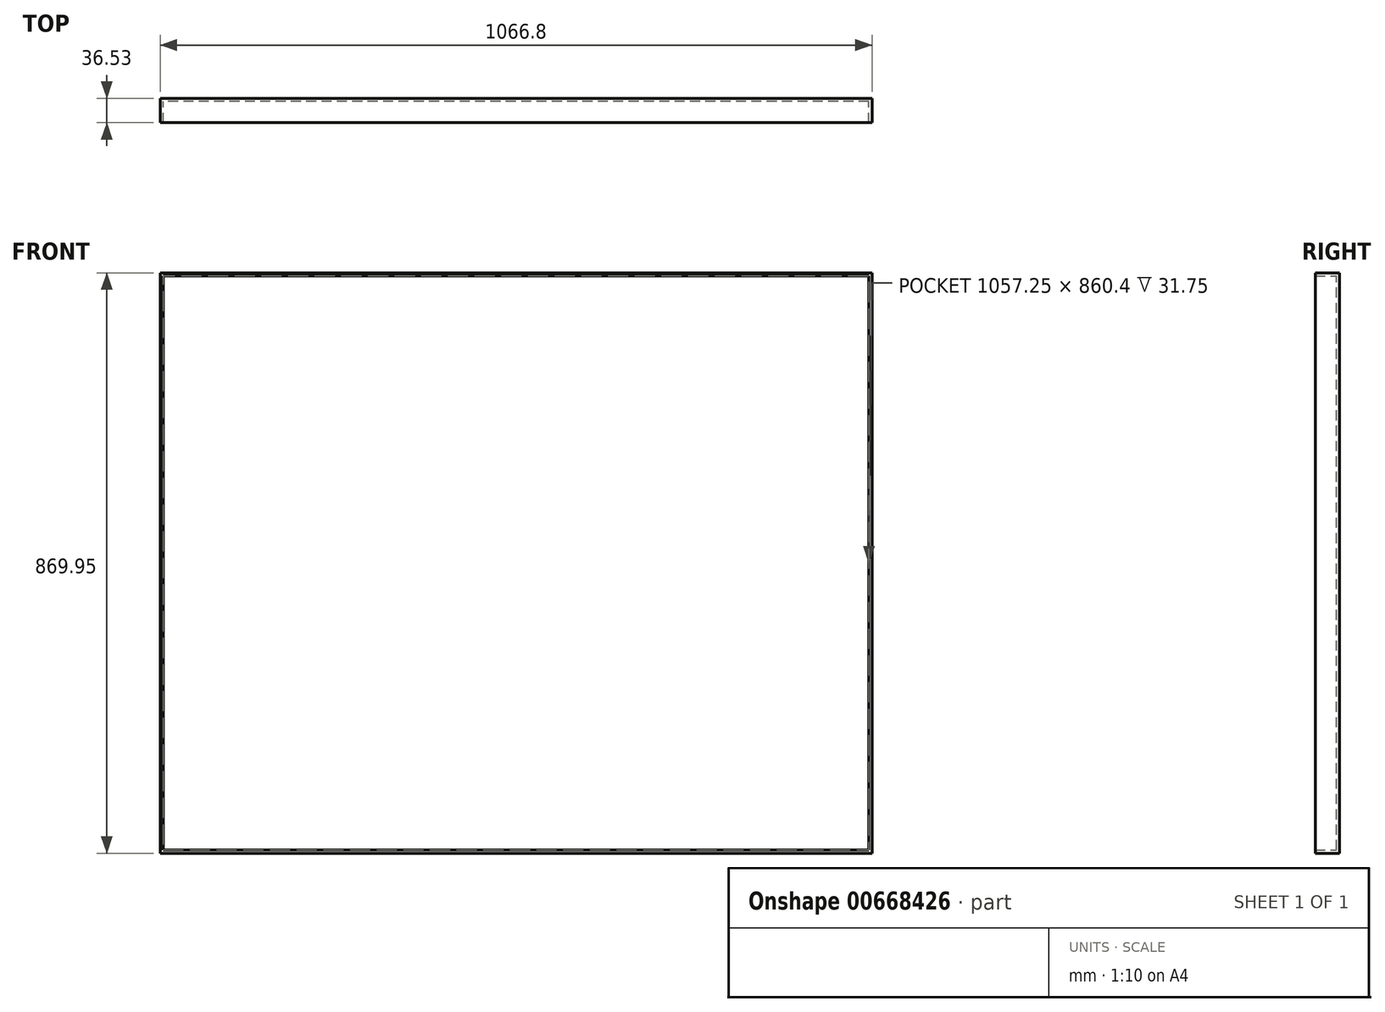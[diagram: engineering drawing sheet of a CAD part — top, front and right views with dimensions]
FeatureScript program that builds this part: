
annotation { "Feature Type Name" : "Feature", "Feature Type Description" : "" }
export const myFeature = defineFeature(function(context is Context, id is Id, definition is map)
    precondition{}
    {
        {
            var Q0;
            Q0=qCreatedBy(makeId("Right.planeOp"),FACE);
            var sketch = newSketch(context, id + "F0", { "sketchPlane" : qUnion([Q0])});
            skLineSegment(sketch, "E0.bottom", {"start": v(-51.66, -73.82) * mm, "end": v(-46.88, -73.82) * mm});
            skLineSegment(sketch, "E0.top", {"start": v(-51.66, 796.13) * mm, "end": v(-46.88, 796.13) * mm});
            skLineSegment(sketch, "E0.left", {"start": v(-51.66, -73.82) * mm, "end": v(-51.66, 796.13) * mm});
            skLineSegment(sketch, "E0.right", {"start": v(-46.88, -73.82) * mm, "end": v(-46.88, 796.13) * mm});
            skSolve(sketch);
        }
        {
            var Q0;
            Q0 = qSketchRegion(id + "F0", true);
            extrude(context, id + "F1", {"entities" : qUnion([Q0]), "depth" : 1066.8 * mm, "offsetDistance" : 25.4 * mm});
        }
        {
            var Q0;
            Q0=makeQuery(id+"F1.opExtrude","SWEPT_FACE",FACE,{"disambiguationData":[OSD([sQuery(id+"F0.wireOp",EDGE,"E0.left")])]});
            var sketch = newSketch(context, id + "F2", { "sketchPlane" : qUnion([Q0])});
            skLineSegment(sketch, "E1.bottom", {"start": v(0, -73.82) * mm, "end": v(4.78, -73.82) * mm});
            skLineSegment(sketch, "E1.top", {"start": v(0, 796.13) * mm, "end": v(4.78, 796.13) * mm});
            skLineSegment(sketch, "E1.left", {"start": v(0, -73.82) * mm, "end": v(0, 796.13) * mm});
            skLineSegment(sketch, "E1.right", {"start": v(4.78, -73.82) * mm, "end": v(4.78, 796.13) * mm});
            skLineSegment(sketch, "E2.bottom", {"start": v(1066.8, -73.82) * mm, "end": v(1062.02, -73.82) * mm});
            skLineSegment(sketch, "E2.top", {"start": v(1066.8, 796.13) * mm, "end": v(1062.02, 796.13) * mm});
            skLineSegment(sketch, "E3.left", {"start": v(1066.8, -73.82) * mm, "end": v(1066.8, 796.13) * mm});
            skLineSegment(sketch, "E3.right", {"start": v(1062.02, -73.82) * mm, "end": v(1062.02, 796.13) * mm});
            skLineSegment(sketch, "E4.bottom", {"start": v(1066.8, -73.82) * mm, "end": v(0, -73.82) * mm});
            skLineSegment(sketch, "E4.top", {"start": v(1066.8, -69.05) * mm, "end": v(0, -69.05) * mm});
            skLineSegment(sketch, "E4.left", {"start": v(1066.8, -73.82) * mm, "end": v(1066.8, -69.05) * mm});
            skLineSegment(sketch, "E4.right", {"start": v(0, -73.82) * mm, "end": v(0, -69.05) * mm});
            skLineSegment(sketch, "E5.bottom", {"start": v(0, 796.13) * mm, "end": v(1066.8, 796.13) * mm});
            skLineSegment(sketch, "E5.top", {"start": v(0, 791.35) * mm, "end": v(1066.8, 791.35) * mm});
            skLineSegment(sketch, "E5.left", {"start": v(0, 796.13) * mm, "end": v(0, 791.35) * mm});
            skLineSegment(sketch, "E5.right", {"start": v(1066.8, 796.13) * mm, "end": v(1066.8, 791.35) * mm});
            skSolve(sketch);
        }
        {
            var Q0;
            Q0 = qSketchRegion(id + "F2", true);
            extrude(context, id + "F3", {"entities" : qUnion([Q0]), "operationType" : NewBodyOperationType.ADD, "depth" : 31.75 * mm, "offsetDistance" : 25.4 * mm});
        }
    });
